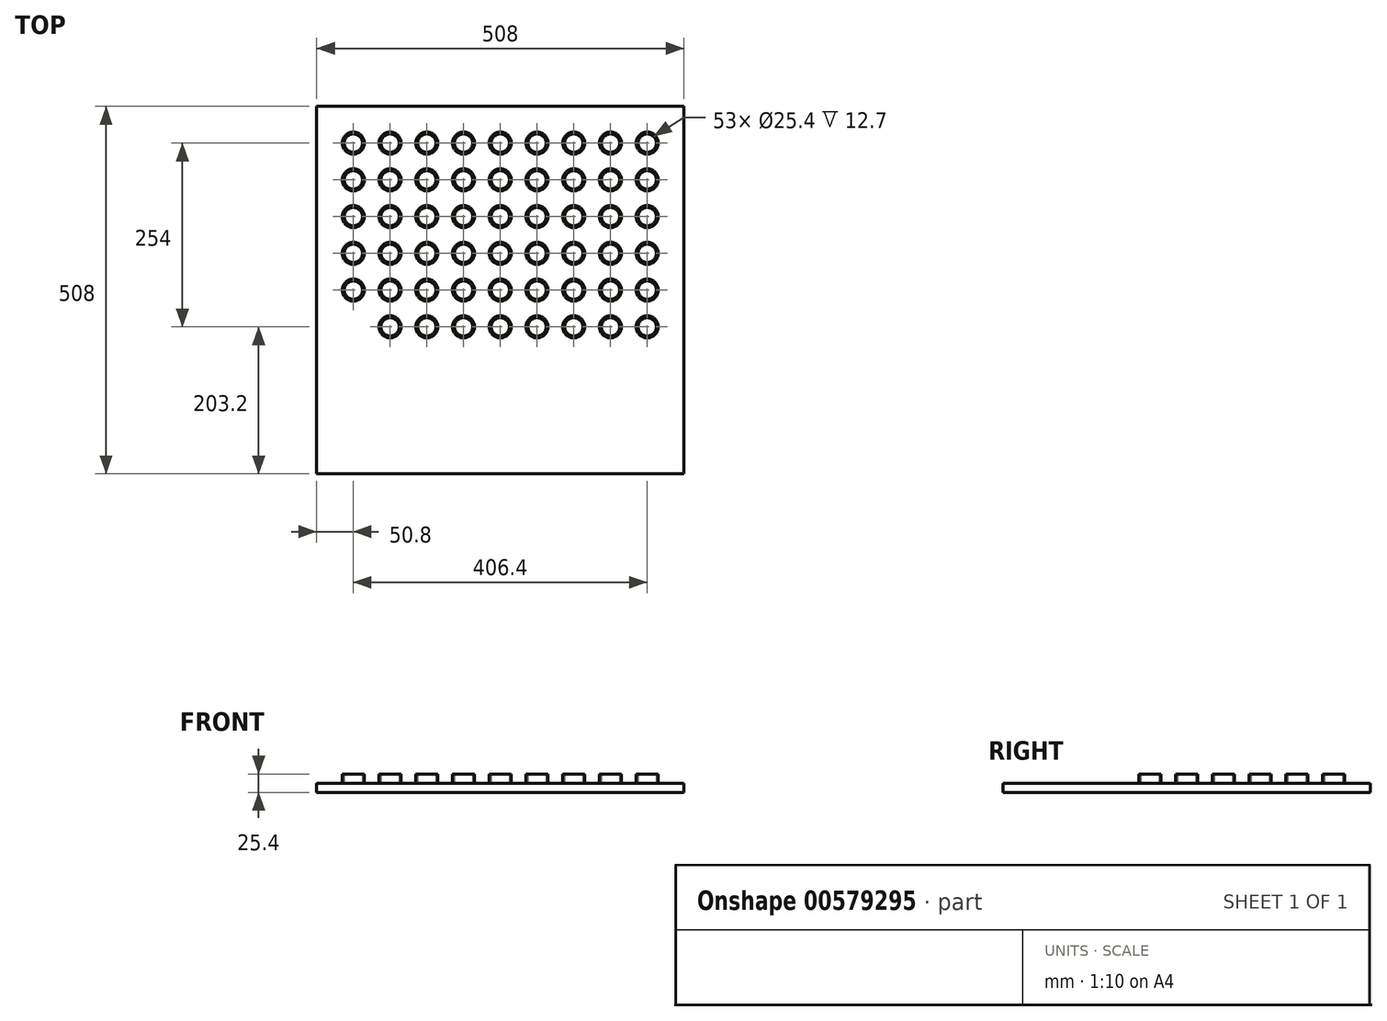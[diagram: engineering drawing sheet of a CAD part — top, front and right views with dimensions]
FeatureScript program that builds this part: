
annotation { "Feature Type Name" : "Feature", "Feature Type Description" : "" }
export const myFeature = defineFeature(function(context is Context, id is Id, definition is map)
    precondition{}
    {
        {
            var Q0;
            Q0=qCreatedBy(makeId("Top.planeOp"),FACE);
            var sketch = newSketch(context, id + "F0", { "sketchPlane" : qUnion([Q0])});
            skLineSegment(sketch, "E0.bottom", {"start": v(-254, 254) * mm, "end": v(254, 254) * mm});
            skLineSegment(sketch, "E0.top", {"start": v(-254, -254) * mm, "end": v(254, -254) * mm});
            skLineSegment(sketch, "E0.left", {"start": v(-254, 254) * mm, "end": v(-254, -254) * mm});
            skLineSegment(sketch, "E0.right", {"start": v(254, 254) * mm, "end": v(254, -254) * mm});
            skPoint(sketch, "E0.middle", {"position": v(0, 0) * mm});
            skSolve(sketch);
        }
        {
            var Q0;
            Q0=makeQuery(id+"F0.imprint","IMPRINT",FACE,{"disambiguationData":[TD([[makeQuery(id+"F0.imprint","IMPRINT",EDGE,{"derivedFrom":sQuery(id+"F0.wireOp",EDGE,"E0.bottom")}),-1.0]])]});
            extrude(context, id + "F1", {"entities" : qUnion([Q0]), "depth" : 12.7 * mm, "offsetDistance" : 25.4 * mm});
        }
        {
            var Q0;
            Q0=qCreatedBy(makeId("Top.planeOp"),FACE);
            var sketch = newSketch(context, id + "F2", { "sketchPlane" : qUnion([Q0])});
            skCircle(sketch, "E1", {"center": v(-203.2, 203.2) * mm, "radius": 12.7 * mm});
            skCircle(sketch, "E2.0", {"center": v(-203.2, 203.2) * mm, "radius": 15.24 * mm});
            skCircle(sketch, "E3.0.1.0", {"center": v(-203.2, 152.4) * mm, "radius": 15.24 * mm});
            skCircle(sketch, "E3.0.1.1", {"center": v(-203.2, 152.4) * mm, "radius": 12.7 * mm});
            skCircle(sketch, "E3.0.2.0", {"center": v(-203.2, 101.6) * mm, "radius": 15.24 * mm});
            skCircle(sketch, "E3.0.2.1", {"center": v(-203.2, 101.6) * mm, "radius": 12.7 * mm});
            skCircle(sketch, "E3.0.3.0", {"center": v(-203.2, 50.8) * mm, "radius": 15.24 * mm});
            skCircle(sketch, "E3.0.3.1", {"center": v(-203.2, 50.8) * mm, "radius": 12.7 * mm});
            skCircle(sketch, "E3.0.4.0", {"center": v(-203.2, 0) * mm, "radius": 15.24 * mm});
            skCircle(sketch, "E3.0.4.1", {"center": v(-203.2, 0) * mm, "radius": 12.7 * mm});
            skCircle(sketch, "E3.0.5.0", {"center": v(-203.2, -50.8) * mm, "radius": 15.24 * mm});
            skCircle(sketch, "E3.0.5.1", {"center": v(-203.2, -50.8) * mm, "radius": 12.7 * mm});
            skCircle(sketch, "E3.0.6.0", {"center": v(-203.2, -101.6) * mm, "radius": 15.24 * mm});
            skCircle(sketch, "E3.0.6.1", {"center": v(-203.2, -101.6) * mm, "radius": 12.7 * mm});
            skCircle(sketch, "E3.0.7.0", {"center": v(-203.2, -152.4) * mm, "radius": 15.24 * mm});
            skCircle(sketch, "E3.0.7.1", {"center": v(-203.2, -152.4) * mm, "radius": 12.7 * mm});
            skCircle(sketch, "E3.0.8.0", {"center": v(-203.2, -203.2) * mm, "radius": 15.24 * mm});
            skCircle(sketch, "E3.0.8.1", {"center": v(-203.2, -203.2) * mm, "radius": 12.7 * mm});
            skCircle(sketch, "E3.1.0.0", {"center": v(-152.4, 203.2) * mm, "radius": 15.24 * mm});
            skCircle(sketch, "E3.1.0.1", {"center": v(-152.4, 203.2) * mm, "radius": 12.7 * mm});
            skCircle(sketch, "E3.1.1.0", {"center": v(-152.4, 152.4) * mm, "radius": 15.24 * mm});
            skCircle(sketch, "E3.1.1.1", {"center": v(-152.4, 152.4) * mm, "radius": 12.7 * mm});
            skCircle(sketch, "E3.1.2.0", {"center": v(-152.4, 101.6) * mm, "radius": 15.24 * mm});
            skCircle(sketch, "E3.1.2.1", {"center": v(-152.4, 101.6) * mm, "radius": 12.7 * mm});
            skCircle(sketch, "E3.1.3.0", {"center": v(-152.4, 50.8) * mm, "radius": 15.24 * mm});
            skCircle(sketch, "E3.1.3.1", {"center": v(-152.4, 50.8) * mm, "radius": 12.7 * mm});
            skCircle(sketch, "E3.1.4.0", {"center": v(-152.4, 0) * mm, "radius": 15.24 * mm});
            skCircle(sketch, "E3.1.4.1", {"center": v(-152.4, 0) * mm, "radius": 12.7 * mm});
            skCircle(sketch, "E3.1.5.0", {"center": v(-152.4, -50.8) * mm, "radius": 15.24 * mm});
            skCircle(sketch, "E3.1.5.1", {"center": v(-152.4, -50.8) * mm, "radius": 12.7 * mm});
            skCircle(sketch, "E3.1.6.0", {"center": v(-152.4, -101.6) * mm, "radius": 15.24 * mm});
            skCircle(sketch, "E3.1.6.1", {"center": v(-152.4, -101.6) * mm, "radius": 12.7 * mm});
            skCircle(sketch, "E3.1.7.0", {"center": v(-152.4, -152.4) * mm, "radius": 15.24 * mm});
            skCircle(sketch, "E3.1.7.1", {"center": v(-152.4, -152.4) * mm, "radius": 12.7 * mm});
            skCircle(sketch, "E3.1.8.0", {"center": v(-152.4, -203.2) * mm, "radius": 15.24 * mm});
            skCircle(sketch, "E3.1.8.1", {"center": v(-152.4, -203.2) * mm, "radius": 12.7 * mm});
            skCircle(sketch, "E3.2.0.0", {"center": v(-101.6, 203.2) * mm, "radius": 15.24 * mm});
            skCircle(sketch, "E3.2.0.1", {"center": v(-101.6, 203.2) * mm, "radius": 12.7 * mm});
            skCircle(sketch, "E3.2.1.0", {"center": v(-101.6, 152.4) * mm, "radius": 15.24 * mm});
            skCircle(sketch, "E3.2.1.1", {"center": v(-101.6, 152.4) * mm, "radius": 12.7 * mm});
            skCircle(sketch, "E3.2.2.0", {"center": v(-101.6, 101.6) * mm, "radius": 15.24 * mm});
            skCircle(sketch, "E3.2.2.1", {"center": v(-101.6, 101.6) * mm, "radius": 12.7 * mm});
            skCircle(sketch, "E3.2.3.0", {"center": v(-101.6, 50.8) * mm, "radius": 15.24 * mm});
            skCircle(sketch, "E3.2.3.1", {"center": v(-101.6, 50.8) * mm, "radius": 12.7 * mm});
            skCircle(sketch, "E3.2.4.0", {"center": v(-101.6, 0) * mm, "radius": 15.24 * mm});
            skCircle(sketch, "E3.2.4.1", {"center": v(-101.6, 0) * mm, "radius": 12.7 * mm});
            skCircle(sketch, "E3.2.5.0", {"center": v(-101.6, -50.8) * mm, "radius": 15.24 * mm});
            skCircle(sketch, "E3.2.5.1", {"center": v(-101.6, -50.8) * mm, "radius": 12.7 * mm});
            skCircle(sketch, "E3.2.6.0", {"center": v(-101.6, -101.6) * mm, "radius": 15.24 * mm});
            skCircle(sketch, "E3.2.6.1", {"center": v(-101.6, -101.6) * mm, "radius": 12.7 * mm});
            skCircle(sketch, "E3.2.7.0", {"center": v(-101.6, -152.4) * mm, "radius": 15.24 * mm});
            skCircle(sketch, "E3.2.7.1", {"center": v(-101.6, -152.4) * mm, "radius": 12.7 * mm});
            skCircle(sketch, "E3.2.8.0", {"center": v(-101.6, -203.2) * mm, "radius": 15.24 * mm});
            skCircle(sketch, "E3.2.8.1", {"center": v(-101.6, -203.2) * mm, "radius": 12.7 * mm});
            skCircle(sketch, "E3.3.0.0", {"center": v(-50.8, 203.2) * mm, "radius": 15.24 * mm});
            skCircle(sketch, "E3.3.0.1", {"center": v(-50.8, 203.2) * mm, "radius": 12.7 * mm});
            skCircle(sketch, "E3.3.1.0", {"center": v(-50.8, 152.4) * mm, "radius": 15.24 * mm});
            skCircle(sketch, "E3.3.1.1", {"center": v(-50.8, 152.4) * mm, "radius": 12.7 * mm});
            skCircle(sketch, "E3.3.2.0", {"center": v(-50.8, 101.6) * mm, "radius": 15.24 * mm});
            skCircle(sketch, "E3.3.2.1", {"center": v(-50.8, 101.6) * mm, "radius": 12.7 * mm});
            skCircle(sketch, "E3.3.3.0", {"center": v(-50.8, 50.8) * mm, "radius": 15.24 * mm});
            skCircle(sketch, "E3.3.3.1", {"center": v(-50.8, 50.8) * mm, "radius": 12.7 * mm});
            skCircle(sketch, "E3.3.4.0", {"center": v(-50.8, 0) * mm, "radius": 15.24 * mm});
            skCircle(sketch, "E3.3.4.1", {"center": v(-50.8, 0) * mm, "radius": 12.7 * mm});
            skCircle(sketch, "E3.3.5.0", {"center": v(-50.8, -50.8) * mm, "radius": 15.24 * mm});
            skCircle(sketch, "E3.3.5.1", {"center": v(-50.8, -50.8) * mm, "radius": 12.7 * mm});
            skCircle(sketch, "E3.3.6.0", {"center": v(-50.8, -101.6) * mm, "radius": 15.24 * mm});
            skCircle(sketch, "E3.3.6.1", {"center": v(-50.8, -101.6) * mm, "radius": 12.7 * mm});
            skCircle(sketch, "E3.3.7.0", {"center": v(-50.8, -152.4) * mm, "radius": 15.24 * mm});
            skCircle(sketch, "E3.3.7.1", {"center": v(-50.8, -152.4) * mm, "radius": 12.7 * mm});
            skCircle(sketch, "E3.3.8.0", {"center": v(-50.8, -203.2) * mm, "radius": 15.24 * mm});
            skCircle(sketch, "E3.3.8.1", {"center": v(-50.8, -203.2) * mm, "radius": 12.7 * mm});
            skCircle(sketch, "E3.4.0.0", {"center": v(0, 203.2) * mm, "radius": 15.24 * mm});
            skCircle(sketch, "E3.4.0.1", {"center": v(0, 203.2) * mm, "radius": 12.7 * mm});
            skCircle(sketch, "E3.4.1.0", {"center": v(0, 152.4) * mm, "radius": 15.24 * mm});
            skCircle(sketch, "E3.4.1.1", {"center": v(0, 152.4) * mm, "radius": 12.7 * mm});
            skCircle(sketch, "E3.4.2.0", {"center": v(0, 101.6) * mm, "radius": 15.24 * mm});
            skCircle(sketch, "E3.4.2.1", {"center": v(0, 101.6) * mm, "radius": 12.7 * mm});
            skCircle(sketch, "E3.4.3.0", {"center": v(0, 50.8) * mm, "radius": 15.24 * mm});
            skCircle(sketch, "E3.4.3.1", {"center": v(0, 50.8) * mm, "radius": 12.7 * mm});
            skCircle(sketch, "E3.4.4.0", {"center": v(0, 0) * mm, "radius": 15.24 * mm});
            skCircle(sketch, "E3.4.4.1", {"center": v(0, 0) * mm, "radius": 12.7 * mm});
            skCircle(sketch, "E3.4.5.0", {"center": v(0, -50.8) * mm, "radius": 15.24 * mm});
            skCircle(sketch, "E3.4.5.1", {"center": v(0, -50.8) * mm, "radius": 12.7 * mm});
            skCircle(sketch, "E3.4.6.0", {"center": v(0, -101.6) * mm, "radius": 15.24 * mm});
            skCircle(sketch, "E3.4.6.1", {"center": v(0, -101.6) * mm, "radius": 12.7 * mm});
            skCircle(sketch, "E3.4.7.0", {"center": v(0, -152.4) * mm, "radius": 15.24 * mm});
            skCircle(sketch, "E3.4.7.1", {"center": v(0, -152.4) * mm, "radius": 12.7 * mm});
            skCircle(sketch, "E3.4.8.0", {"center": v(0, -203.2) * mm, "radius": 15.24 * mm});
            skCircle(sketch, "E3.4.8.1", {"center": v(0, -203.2) * mm, "radius": 12.7 * mm});
            skCircle(sketch, "E3.5.0.0", {"center": v(50.8, 203.2) * mm, "radius": 15.24 * mm});
            skCircle(sketch, "E3.5.0.1", {"center": v(50.8, 203.2) * mm, "radius": 12.7 * mm});
            skCircle(sketch, "E3.5.1.0", {"center": v(50.8, 152.4) * mm, "radius": 15.24 * mm});
            skCircle(sketch, "E3.5.1.1", {"center": v(50.8, 152.4) * mm, "radius": 12.7 * mm});
            skCircle(sketch, "E3.5.2.0", {"center": v(50.8, 101.6) * mm, "radius": 15.24 * mm});
            skCircle(sketch, "E3.5.2.1", {"center": v(50.8, 101.6) * mm, "radius": 12.7 * mm});
            skCircle(sketch, "E3.5.3.0", {"center": v(50.8, 50.8) * mm, "radius": 15.24 * mm});
            skCircle(sketch, "E3.5.3.1", {"center": v(50.8, 50.8) * mm, "radius": 12.7 * mm});
            skCircle(sketch, "E3.5.4.0", {"center": v(50.8, 0) * mm, "radius": 15.24 * mm});
            skCircle(sketch, "E3.5.4.1", {"center": v(50.8, 0) * mm, "radius": 12.7 * mm});
            skCircle(sketch, "E3.5.5.0", {"center": v(50.8, -50.8) * mm, "radius": 15.24 * mm});
            skCircle(sketch, "E3.5.5.1", {"center": v(50.8, -50.8) * mm, "radius": 12.7 * mm});
            skCircle(sketch, "E3.5.6.0", {"center": v(50.8, -101.6) * mm, "radius": 15.24 * mm});
            skCircle(sketch, "E3.5.6.1", {"center": v(50.8, -101.6) * mm, "radius": 12.7 * mm});
            skCircle(sketch, "E3.5.7.0", {"center": v(50.8, -152.4) * mm, "radius": 15.24 * mm});
            skCircle(sketch, "E3.5.7.1", {"center": v(50.8, -152.4) * mm, "radius": 12.7 * mm});
            skCircle(sketch, "E3.5.8.0", {"center": v(50.8, -203.2) * mm, "radius": 15.24 * mm});
            skCircle(sketch, "E3.5.8.1", {"center": v(50.8, -203.2) * mm, "radius": 12.7 * mm});
            skCircle(sketch, "E3.6.0.0", {"center": v(101.6, 203.2) * mm, "radius": 15.24 * mm});
            skCircle(sketch, "E3.6.0.1", {"center": v(101.6, 203.2) * mm, "radius": 12.7 * mm});
            skCircle(sketch, "E3.6.1.0", {"center": v(101.6, 152.4) * mm, "radius": 15.24 * mm});
            skCircle(sketch, "E3.6.1.1", {"center": v(101.6, 152.4) * mm, "radius": 12.7 * mm});
            skCircle(sketch, "E3.6.2.0", {"center": v(101.6, 101.6) * mm, "radius": 15.24 * mm});
            skCircle(sketch, "E3.6.2.1", {"center": v(101.6, 101.6) * mm, "radius": 12.7 * mm});
            skCircle(sketch, "E3.6.3.0", {"center": v(101.6, 50.8) * mm, "radius": 15.24 * mm});
            skCircle(sketch, "E3.6.3.1", {"center": v(101.6, 50.8) * mm, "radius": 12.7 * mm});
            skCircle(sketch, "E3.6.4.0", {"center": v(101.6, 0) * mm, "radius": 15.24 * mm});
            skCircle(sketch, "E3.6.4.1", {"center": v(101.6, 0) * mm, "radius": 12.7 * mm});
            skCircle(sketch, "E3.6.5.0", {"center": v(101.6, -50.8) * mm, "radius": 15.24 * mm});
            skCircle(sketch, "E3.6.5.1", {"center": v(101.6, -50.8) * mm, "radius": 12.7 * mm});
            skCircle(sketch, "E3.6.6.0", {"center": v(101.6, -101.6) * mm, "radius": 15.24 * mm});
            skCircle(sketch, "E3.6.6.1", {"center": v(101.6, -101.6) * mm, "radius": 12.7 * mm});
            skCircle(sketch, "E3.6.7.0", {"center": v(101.6, -152.4) * mm, "radius": 15.24 * mm});
            skCircle(sketch, "E3.6.7.1", {"center": v(101.6, -152.4) * mm, "radius": 12.7 * mm});
            skCircle(sketch, "E3.6.8.0", {"center": v(101.6, -203.2) * mm, "radius": 15.24 * mm});
            skCircle(sketch, "E3.6.8.1", {"center": v(101.6, -203.2) * mm, "radius": 12.7 * mm});
            skCircle(sketch, "E3.7.0.0", {"center": v(152.4, 203.2) * mm, "radius": 15.24 * mm});
            skCircle(sketch, "E3.7.0.1", {"center": v(152.4, 203.2) * mm, "radius": 12.7 * mm});
            skCircle(sketch, "E3.7.1.0", {"center": v(152.4, 152.4) * mm, "radius": 15.24 * mm});
            skCircle(sketch, "E3.7.1.1", {"center": v(152.4, 152.4) * mm, "radius": 12.7 * mm});
            skCircle(sketch, "E3.7.2.0", {"center": v(152.4, 101.6) * mm, "radius": 15.24 * mm});
            skCircle(sketch, "E3.7.2.1", {"center": v(152.4, 101.6) * mm, "radius": 12.7 * mm});
            skCircle(sketch, "E3.7.3.0", {"center": v(152.4, 50.8) * mm, "radius": 15.24 * mm});
            skCircle(sketch, "E3.7.3.1", {"center": v(152.4, 50.8) * mm, "radius": 12.7 * mm});
            skCircle(sketch, "E3.7.4.0", {"center": v(152.4, 0) * mm, "radius": 15.24 * mm});
            skCircle(sketch, "E3.7.4.1", {"center": v(152.4, 0) * mm, "radius": 12.7 * mm});
            skCircle(sketch, "E3.7.5.0", {"center": v(152.4, -50.8) * mm, "radius": 15.24 * mm});
            skCircle(sketch, "E3.7.5.1", {"center": v(152.4, -50.8) * mm, "radius": 12.7 * mm});
            skCircle(sketch, "E3.7.6.0", {"center": v(152.4, -101.6) * mm, "radius": 15.24 * mm});
            skCircle(sketch, "E3.7.6.1", {"center": v(152.4, -101.6) * mm, "radius": 12.7 * mm});
            skCircle(sketch, "E3.7.7.0", {"center": v(152.4, -152.4) * mm, "radius": 15.24 * mm});
            skCircle(sketch, "E3.7.7.1", {"center": v(152.4, -152.4) * mm, "radius": 12.7 * mm});
            skCircle(sketch, "E3.7.8.0", {"center": v(152.4, -203.2) * mm, "radius": 15.24 * mm});
            skCircle(sketch, "E3.7.8.1", {"center": v(152.4, -203.2) * mm, "radius": 12.7 * mm});
            skCircle(sketch, "E3.8.0.0", {"center": v(203.2, 203.2) * mm, "radius": 15.24 * mm});
            skCircle(sketch, "E3.8.0.1", {"center": v(203.2, 203.2) * mm, "radius": 12.7 * mm});
            skCircle(sketch, "E3.8.1.0", {"center": v(203.2, 152.4) * mm, "radius": 15.24 * mm});
            skCircle(sketch, "E3.8.1.1", {"center": v(203.2, 152.4) * mm, "radius": 12.7 * mm});
            skCircle(sketch, "E3.8.2.0", {"center": v(203.2, 101.6) * mm, "radius": 15.24 * mm});
            skCircle(sketch, "E3.8.2.1", {"center": v(203.2, 101.6) * mm, "radius": 12.7 * mm});
            skCircle(sketch, "E3.8.3.0", {"center": v(203.2, 50.8) * mm, "radius": 15.24 * mm});
            skCircle(sketch, "E3.8.3.1", {"center": v(203.2, 50.8) * mm, "radius": 12.7 * mm});
            skCircle(sketch, "E3.8.4.0", {"center": v(203.2, 0) * mm, "radius": 15.24 * mm});
            skCircle(sketch, "E3.8.4.1", {"center": v(203.2, 0) * mm, "radius": 12.7 * mm});
            skCircle(sketch, "E3.8.5.0", {"center": v(203.2, -50.8) * mm, "radius": 15.24 * mm});
            skCircle(sketch, "E3.8.5.1", {"center": v(203.2, -50.8) * mm, "radius": 12.7 * mm});
            skCircle(sketch, "E3.8.6.0", {"center": v(203.2, -101.6) * mm, "radius": 15.24 * mm});
            skCircle(sketch, "E3.8.6.1", {"center": v(203.2, -101.6) * mm, "radius": 12.7 * mm});
            skCircle(sketch, "E3.8.7.0", {"center": v(203.2, -152.4) * mm, "radius": 15.24 * mm});
            skCircle(sketch, "E3.8.7.1", {"center": v(203.2, -152.4) * mm, "radius": 12.7 * mm});
            skCircle(sketch, "E3.8.8.0", {"center": v(203.2, -203.2) * mm, "radius": 15.24 * mm});
            skCircle(sketch, "E3.8.8.1", {"center": v(203.2, -203.2) * mm, "radius": 12.7 * mm});
            skLineSegment(sketch, "E3.direction1", {"start": v(-203.2, 203.2) * mm, "end": v(-152.4, 203.2) * mm, "construction": true});
            skLineSegment(sketch, "E3.direction2", {"start": v(-203.2, 203.2) * mm, "end": v(-203.2, 152.4) * mm, "construction": true});
            skSolve(sketch);
        }
        {
            var Q0;
            Q0=makeQuery(id+"F2.imprint","IMPRINT",FACE,{"disambiguationData":[TD([[makeQuery(id+"F2.imprint","IMPRINT",EDGE,{"derivedFrom":sQuery(id+"F2.wireOp",EDGE,"E3.1.0.0")}),1.0]])]});
            var Q1;
            Q1=makeQuery(id+"F2.imprint","IMPRINT",FACE,{"disambiguationData":[TD([[makeQuery(id+"F2.imprint","IMPRINT",EDGE,{"derivedFrom":sQuery(id+"F2.wireOp",EDGE,"E1")}),-1.0]])]});
            var Q2;
            Q2=makeQuery(id+"F2.imprint","IMPRINT",FACE,{"disambiguationData":[TD([[makeQuery(id+"F2.imprint","IMPRINT",EDGE,{"derivedFrom":sQuery(id+"F2.wireOp",EDGE,"E3.2.0.0")}),1.0]])]});
            var Q3;
            Q3=makeQuery(id+"F2.imprint","IMPRINT",FACE,{"disambiguationData":[TD([[makeQuery(id+"F2.imprint","IMPRINT",EDGE,{"derivedFrom":sQuery(id+"F2.wireOp",EDGE,"E3.2.1.0")}),1.0]])]});
            var Q4;
            Q4=makeQuery(id+"F2.imprint","IMPRINT",FACE,{"disambiguationData":[TD([[makeQuery(id+"F2.imprint","IMPRINT",EDGE,{"derivedFrom":sQuery(id+"F2.wireOp",EDGE,"E3.1.1.0")}),1.0]])]});
            var Q5;
            Q5=makeQuery(id+"F2.imprint","IMPRINT",FACE,{"disambiguationData":[TD([[makeQuery(id+"F2.imprint","IMPRINT",EDGE,{"derivedFrom":sQuery(id+"F2.wireOp",EDGE,"E3.0.1.0")}),1.0]])]});
            var Q6;
            Q6=makeQuery(id+"F2.imprint","IMPRINT",FACE,{"disambiguationData":[TD([[makeQuery(id+"F2.imprint","IMPRINT",EDGE,{"derivedFrom":sQuery(id+"F2.wireOp",EDGE,"E3.3.0.0")}),1.0]])]});
            var Q7;
            Q7=makeQuery(id+"F2.imprint","IMPRINT",FACE,{"disambiguationData":[TD([[makeQuery(id+"F2.imprint","IMPRINT",EDGE,{"derivedFrom":sQuery(id+"F2.wireOp",EDGE,"E3.4.0.0")}),1.0]])]});
            var Q8;
            Q8=makeQuery(id+"F2.imprint","IMPRINT",FACE,{"disambiguationData":[TD([[makeQuery(id+"F2.imprint","IMPRINT",EDGE,{"derivedFrom":sQuery(id+"F2.wireOp",EDGE,"E3.5.0.0")}),1.0]])]});
            var Q9;
            Q9=makeQuery(id+"F2.imprint","IMPRINT",FACE,{"disambiguationData":[TD([[makeQuery(id+"F2.imprint","IMPRINT",EDGE,{"derivedFrom":sQuery(id+"F2.wireOp",EDGE,"E3.6.0.0")}),1.0]])]});
            var Q10;
            Q10=makeQuery(id+"F2.imprint","IMPRINT",FACE,{"disambiguationData":[TD([[makeQuery(id+"F2.imprint","IMPRINT",EDGE,{"derivedFrom":sQuery(id+"F2.wireOp",EDGE,"E3.7.0.0")}),1.0]])]});
            var Q11;
            Q11=makeQuery(id+"F2.imprint","IMPRINT",FACE,{"disambiguationData":[TD([[makeQuery(id+"F2.imprint","IMPRINT",EDGE,{"derivedFrom":sQuery(id+"F2.wireOp",EDGE,"E3.8.0.0")}),1.0]])]});
            var Q12;
            Q12=makeQuery(id+"F2.imprint","IMPRINT",FACE,{"disambiguationData":[TD([[makeQuery(id+"F2.imprint","IMPRINT",EDGE,{"derivedFrom":sQuery(id+"F2.wireOp",EDGE,"E3.8.1.0")}),1.0]])]});
            var Q13;
            Q13=makeQuery(id+"F2.imprint","IMPRINT",FACE,{"disambiguationData":[TD([[makeQuery(id+"F2.imprint","IMPRINT",EDGE,{"derivedFrom":sQuery(id+"F2.wireOp",EDGE,"E3.7.1.0")}),1.0]])]});
            var Q14;
            Q14=makeQuery(id+"F2.imprint","IMPRINT",FACE,{"disambiguationData":[TD([[makeQuery(id+"F2.imprint","IMPRINT",EDGE,{"derivedFrom":sQuery(id+"F2.wireOp",EDGE,"E3.6.1.0")}),1.0]])]});
            var Q15;
            Q15=makeQuery(id+"F2.imprint","IMPRINT",FACE,{"disambiguationData":[TD([[makeQuery(id+"F2.imprint","IMPRINT",EDGE,{"derivedFrom":sQuery(id+"F2.wireOp",EDGE,"E3.5.1.0")}),1.0]])]});
            var Q16;
            Q16=makeQuery(id+"F2.imprint","IMPRINT",FACE,{"disambiguationData":[TD([[makeQuery(id+"F2.imprint","IMPRINT",EDGE,{"derivedFrom":sQuery(id+"F2.wireOp",EDGE,"E3.4.1.0")}),1.0]])]});
            var Q17;
            Q17=makeQuery(id+"F2.imprint","IMPRINT",FACE,{"disambiguationData":[TD([[makeQuery(id+"F2.imprint","IMPRINT",EDGE,{"derivedFrom":sQuery(id+"F2.wireOp",EDGE,"E3.3.1.0")}),1.0]])]});
            var Q18;
            Q18=makeQuery(id+"F2.imprint","IMPRINT",FACE,{"disambiguationData":[TD([[makeQuery(id+"F2.imprint","IMPRINT",EDGE,{"derivedFrom":sQuery(id+"F2.wireOp",EDGE,"E3.0.2.0")}),1.0]])]});
            var Q19;
            Q19=makeQuery(id+"F2.imprint","IMPRINT",FACE,{"disambiguationData":[TD([[makeQuery(id+"F2.imprint","IMPRINT",EDGE,{"derivedFrom":sQuery(id+"F2.wireOp",EDGE,"E3.1.2.0")}),1.0]])]});
            var Q20;
            Q20=makeQuery(id+"F2.imprint","IMPRINT",FACE,{"disambiguationData":[TD([[makeQuery(id+"F2.imprint","IMPRINT",EDGE,{"derivedFrom":sQuery(id+"F2.wireOp",EDGE,"E3.2.2.0")}),1.0]])]});
            var Q21;
            Q21=makeQuery(id+"F2.imprint","IMPRINT",FACE,{"disambiguationData":[TD([[makeQuery(id+"F2.imprint","IMPRINT",EDGE,{"derivedFrom":sQuery(id+"F2.wireOp",EDGE,"E3.3.2.0")}),1.0]])]});
            var Q22;
            Q22=makeQuery(id+"F2.imprint","IMPRINT",FACE,{"disambiguationData":[TD([[makeQuery(id+"F2.imprint","IMPRINT",EDGE,{"derivedFrom":sQuery(id+"F2.wireOp",EDGE,"E3.4.2.0")}),1.0]])]});
            var Q23;
            Q23=makeQuery(id+"F2.imprint","IMPRINT",FACE,{"disambiguationData":[TD([[makeQuery(id+"F2.imprint","IMPRINT",EDGE,{"derivedFrom":sQuery(id+"F2.wireOp",EDGE,"E3.5.2.0")}),1.0]])]});
            var Q24;
            Q24=makeQuery(id+"F2.imprint","IMPRINT",FACE,{"disambiguationData":[TD([[makeQuery(id+"F2.imprint","IMPRINT",EDGE,{"derivedFrom":sQuery(id+"F2.wireOp",EDGE,"E3.6.2.0")}),1.0]])]});
            var Q25;
            Q25=makeQuery(id+"F2.imprint","IMPRINT",FACE,{"disambiguationData":[TD([[makeQuery(id+"F2.imprint","IMPRINT",EDGE,{"derivedFrom":sQuery(id+"F2.wireOp",EDGE,"E3.7.2.0")}),1.0]])]});
            var Q26;
            Q26=makeQuery(id+"F2.imprint","IMPRINT",FACE,{"disambiguationData":[TD([[makeQuery(id+"F2.imprint","IMPRINT",EDGE,{"derivedFrom":sQuery(id+"F2.wireOp",EDGE,"E3.8.2.0")}),1.0]])]});
            var Q27;
            Q27=makeQuery(id+"F2.imprint","IMPRINT",FACE,{"disambiguationData":[TD([[makeQuery(id+"F2.imprint","IMPRINT",EDGE,{"derivedFrom":sQuery(id+"F2.wireOp",EDGE,"E3.8.3.0")}),1.0]])]});
            var Q28;
            Q28=makeQuery(id+"F2.imprint","IMPRINT",FACE,{"disambiguationData":[TD([[makeQuery(id+"F2.imprint","IMPRINT",EDGE,{"derivedFrom":sQuery(id+"F2.wireOp",EDGE,"E3.7.3.0")}),1.0]])]});
            var Q29;
            Q29=makeQuery(id+"F2.imprint","IMPRINT",FACE,{"disambiguationData":[TD([[makeQuery(id+"F2.imprint","IMPRINT",EDGE,{"derivedFrom":sQuery(id+"F2.wireOp",EDGE,"E3.6.3.0")}),1.0]])]});
            var Q30;
            Q30=makeQuery(id+"F2.imprint","IMPRINT",FACE,{"disambiguationData":[TD([[makeQuery(id+"F2.imprint","IMPRINT",EDGE,{"derivedFrom":sQuery(id+"F2.wireOp",EDGE,"E3.5.3.0")}),1.0]])]});
            var Q31;
            Q31=makeQuery(id+"F2.imprint","IMPRINT",FACE,{"disambiguationData":[TD([[makeQuery(id+"F2.imprint","IMPRINT",EDGE,{"derivedFrom":sQuery(id+"F2.wireOp",EDGE,"E3.4.3.0")}),1.0]])]});
            var Q32;
            Q32=makeQuery(id+"F2.imprint","IMPRINT",FACE,{"disambiguationData":[TD([[makeQuery(id+"F2.imprint","IMPRINT",EDGE,{"derivedFrom":sQuery(id+"F2.wireOp",EDGE,"E3.3.3.0")}),1.0]])]});
            var Q33;
            Q33=makeQuery(id+"F2.imprint","IMPRINT",FACE,{"disambiguationData":[TD([[makeQuery(id+"F2.imprint","IMPRINT",EDGE,{"derivedFrom":sQuery(id+"F2.wireOp",EDGE,"E3.2.3.0")}),1.0]])]});
            var Q34;
            Q34=makeQuery(id+"F2.imprint","IMPRINT",FACE,{"disambiguationData":[TD([[makeQuery(id+"F2.imprint","IMPRINT",EDGE,{"derivedFrom":sQuery(id+"F2.wireOp",EDGE,"E3.1.3.0")}),1.0]])]});
            var Q35;
            Q35=makeQuery(id+"F2.imprint","IMPRINT",FACE,{"disambiguationData":[TD([[makeQuery(id+"F2.imprint","IMPRINT",EDGE,{"derivedFrom":sQuery(id+"F2.wireOp",EDGE,"E3.0.3.0")}),1.0]])]});
            var Q36;
            Q36=makeQuery(id+"F2.imprint","IMPRINT",FACE,{"disambiguationData":[TD([[makeQuery(id+"F2.imprint","IMPRINT",EDGE,{"derivedFrom":sQuery(id+"F2.wireOp",EDGE,"E3.0.4.0")}),1.0]])]});
            var Q37;
            Q37=makeQuery(id+"F2.imprint","IMPRINT",FACE,{"disambiguationData":[TD([[makeQuery(id+"F2.imprint","IMPRINT",EDGE,{"derivedFrom":sQuery(id+"F2.wireOp",EDGE,"E3.1.4.0")}),1.0]])]});
            var Q38;
            Q38=makeQuery(id+"F2.imprint","IMPRINT",FACE,{"disambiguationData":[TD([[makeQuery(id+"F2.imprint","IMPRINT",EDGE,{"derivedFrom":sQuery(id+"F2.wireOp",EDGE,"E3.2.4.0")}),1.0]])]});
            var Q39;
            Q39=makeQuery(id+"F2.imprint","IMPRINT",FACE,{"disambiguationData":[TD([[makeQuery(id+"F2.imprint","IMPRINT",EDGE,{"derivedFrom":sQuery(id+"F2.wireOp",EDGE,"E3.3.4.0")}),1.0]])]});
            var Q40;
            Q40=makeQuery(id+"F2.imprint","IMPRINT",FACE,{"disambiguationData":[TD([[makeQuery(id+"F2.imprint","IMPRINT",EDGE,{"derivedFrom":sQuery(id+"F2.wireOp",EDGE,"E3.4.4.0")}),1.0]])]});
            var Q41;
            Q41=makeQuery(id+"F2.imprint","IMPRINT",FACE,{"disambiguationData":[TD([[makeQuery(id+"F2.imprint","IMPRINT",EDGE,{"derivedFrom":sQuery(id+"F2.wireOp",EDGE,"E3.5.4.0")}),1.0]])]});
            var Q42;
            Q42=makeQuery(id+"F2.imprint","IMPRINT",FACE,{"disambiguationData":[TD([[makeQuery(id+"F2.imprint","IMPRINT",EDGE,{"derivedFrom":sQuery(id+"F2.wireOp",EDGE,"E3.6.4.0")}),1.0]])]});
            var Q43;
            Q43=makeQuery(id+"F2.imprint","IMPRINT",FACE,{"disambiguationData":[TD([[makeQuery(id+"F2.imprint","IMPRINT",EDGE,{"derivedFrom":sQuery(id+"F2.wireOp",EDGE,"E3.7.4.0")}),1.0]])]});
            var Q44;
            Q44=makeQuery(id+"F2.imprint","IMPRINT",FACE,{"disambiguationData":[TD([[makeQuery(id+"F2.imprint","IMPRINT",EDGE,{"derivedFrom":sQuery(id+"F2.wireOp",EDGE,"E3.8.4.0")}),1.0]])]});
            var Q45;
            Q45=makeQuery(id+"F2.imprint","IMPRINT",FACE,{"disambiguationData":[TD([[makeQuery(id+"F2.imprint","IMPRINT",EDGE,{"derivedFrom":sQuery(id+"F2.wireOp",EDGE,"E3.8.5.0")}),1.0]])]});
            var Q46;
            Q46=makeQuery(id+"F2.imprint","IMPRINT",FACE,{"disambiguationData":[TD([[makeQuery(id+"F2.imprint","IMPRINT",EDGE,{"derivedFrom":sQuery(id+"F2.wireOp",EDGE,"E3.7.5.0")}),1.0]])]});
            var Q47;
            Q47=makeQuery(id+"F2.imprint","IMPRINT",FACE,{"disambiguationData":[TD([[makeQuery(id+"F2.imprint","IMPRINT",EDGE,{"derivedFrom":sQuery(id+"F2.wireOp",EDGE,"E3.6.5.0")}),1.0]])]});
            var Q48;
            Q48=makeQuery(id+"F2.imprint","IMPRINT",FACE,{"disambiguationData":[TD([[makeQuery(id+"F2.imprint","IMPRINT",EDGE,{"derivedFrom":sQuery(id+"F2.wireOp",EDGE,"E3.5.5.0")}),1.0]])]});
            var Q49;
            Q49=makeQuery(id+"F2.imprint","IMPRINT",FACE,{"disambiguationData":[TD([[makeQuery(id+"F2.imprint","IMPRINT",EDGE,{"derivedFrom":sQuery(id+"F2.wireOp",EDGE,"E3.4.5.0")}),1.0]])]});
            var Q50;
            Q50=makeQuery(id+"F2.imprint","IMPRINT",FACE,{"disambiguationData":[TD([[makeQuery(id+"F2.imprint","IMPRINT",EDGE,{"derivedFrom":sQuery(id+"F2.wireOp",EDGE,"E3.3.5.0")}),1.0]])]});
            var Q51;
            Q51=makeQuery(id+"F2.imprint","IMPRINT",FACE,{"disambiguationData":[TD([[makeQuery(id+"F2.imprint","IMPRINT",EDGE,{"derivedFrom":sQuery(id+"F2.wireOp",EDGE,"E3.2.5.0")}),1.0]])]});
            var Q52;
            Q52=makeQuery(id+"F2.imprint","IMPRINT",FACE,{"disambiguationData":[TD([[makeQuery(id+"F2.imprint","IMPRINT",EDGE,{"derivedFrom":sQuery(id+"F2.wireOp",EDGE,"E3.1.5.0")}),1.0]])]});
            extrude(context, id + "F3", {"entities" : qUnion([Q0, Q1, Q2, Q3, Q4, Q5, Q6, Q7, Q8, Q9, Q10, Q11, Q12, Q13, Q14, Q15, Q16, Q17, Q18, Q19, Q20, Q21, Q22, Q23, Q24, Q25, Q26, Q27, Q28, Q29, Q30, Q31, Q32, Q33, Q34, Q35, Q36, Q37, Q38, Q39, Q40, Q41, Q42, Q43, Q44, Q45, Q46, Q47, Q48, Q49, Q50, Q51, Q52]), "operationType" : NewBodyOperationType.ADD, "depth" : 25.4 * mm, "offsetDistance" : 25.4 * mm});
        }
    });
